# Revit family: LOROWERK 01367-100X
name_source: partatom
category: Sanitärinstallationen
revit_build: Autodesk Revit 2017 (Build: 20160225_1515(x64)
units: mm (PartAtom-declared; Revit-internal decimal feet)

## family parameters
Arbeitsebenenbasiert = Nein
Beim Laden mit Abzugskörper schneiden = Nein
Bemaßung runder Anschluss = Durchmesser verwenden
Gemeinsam genutzt = Nein
Immer vertikal = Ja
Raumberechnungspunkt = Nein
Teiletyp = Normal

## types (1)
- LOROWERK 01367-100X
    38.710.01.13 = seitlich
    38.710.01.5 = DN
    Abdichtvarianten = mit Klemmflansch
    Abflussstutzen Ausführung = waagerecht
    Ablaufanschluss = 1
    Art der Nenn-/ Betriebsspannung = nicht zutreffend
    Beschreibung = LORO-RAINSTAR Attikaabläufe, Serie 89, Eingrifftiefe 55 mm
    Bestellmenge (Multiplikator) = 1
    CONNECTOR0_DIAMETER_dZ_0r = 100 mm  [stored 0.328084 ft]
    CONNECTOR0_dZ_00 = 67 mm
    CONNECTOR0_dZ_01 = 67 mm
    CONNECTOR0_ref_dZ = 67 mm
    CONNECTOR1_DIAMETER_dNBN0_0r = 100 mm  [stored 0.328084 ft]
    CONNECTOR1_dNBN0_00 = 528 mm
    CONNECTOR1_dNBN0_01 = 602 mm
    CONNECTOR1_ref_dNBN0 = 528 mm
    CONNECTOR1_ref_dNBN1 = 15 mm
    DATANORM = 01367.100X
    Einbaubreite [mm] = 215
    Einbautiefe [mm] = 55
    Elektrischer Anschluss = nein
    Feuerwiderstandsklasse = keine Feuerwiderstandsklasse
    Feuerwiderstandsklasse nachrüstbar = nein
    GTIN = 4038088074817
    Gehäuseanschlussarten = Ablauf punktförmig
    Geruchsverschluss = ohne Geruchsverschluss
    HAN = 01367.100X
    HeinzeBIM = https://www.heinze.de
    Heizung = ohne Heizung
    Hersteller = LOROWERK K.H. Vahlbrauk GmbH & Co. KG
    Kommentar = Serie 89, Eingrifftiefe 55 mm
    LOROWERK 01367.100X en Visibility = Ja
    Nenndruck = 738
    Nenndrucksystem = 270
    Nennweitensystem = PN
    Potenzialausgleich (Erdungsanschluss)   vorhanden = ja
    Produktbezeichnung = Dachabläufe und Bodenabläufe ohne Geruchverschluss
    Produktbezeichnung Text = LORO-RAINSTAR 89 Attikanotablauf, Einbau 55mm, Edelst., Klemmfl., f. Kunstst.-bahn, Druckström., DN100
    Produktklassifikation = Attikaablauf
    Produktname = LORO-RAINSTAR 89 Attikanotablauf, Einbau 55mm, Edelst., Klemmfl., f. Kunstst.-bahn, Druckström., DN100
    Sperrwasserhöhe [mm] = 0
    Typname = LORO-RAINSTAR 89 Attikanotablauf, Einbau 55mm, Edelst., Klemmfl., f. Kunstst.-bahn, Druckström., DN100
    VDIBSN = 0020080000020020000010020010010000000030020000001600000001
    Werkstoff des Ablaufkörpers = nicht rostender Stahl
    Wärmedämmung = ohne Wärmedämmung

note: [stored X ft] marks values corroborated as IEEE doubles in the binary element streams (Revit-internal decimal feet)
